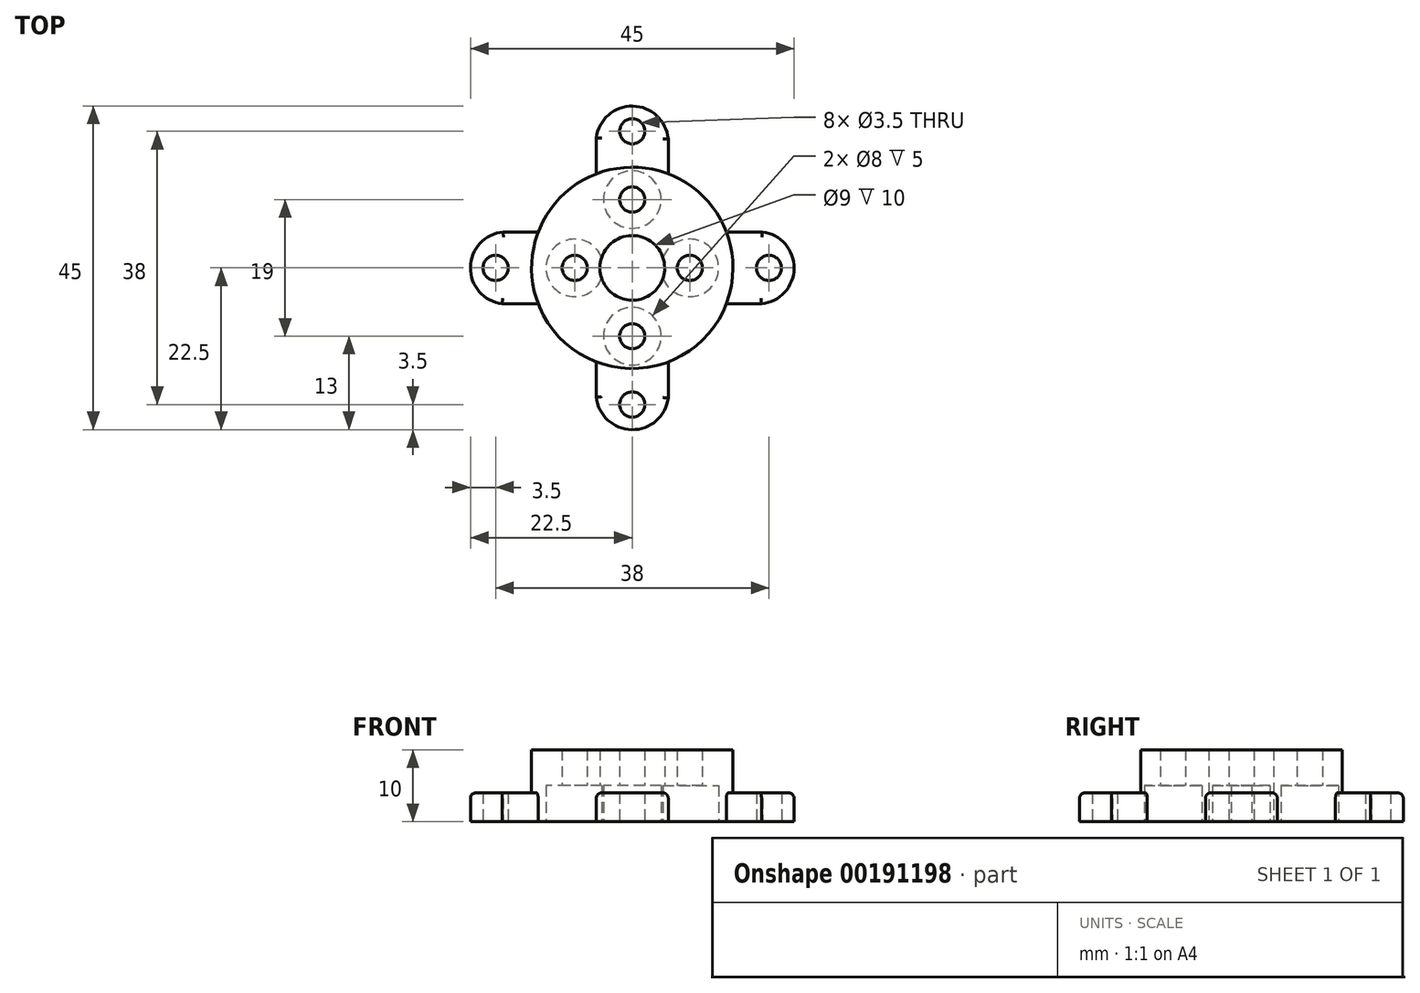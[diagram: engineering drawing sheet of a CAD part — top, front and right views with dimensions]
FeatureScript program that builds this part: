
annotation { "Feature Type Name" : "Feature", "Feature Type Description" : "" }
export const myFeature = defineFeature(function(context is Context, id is Id, definition is map)
    precondition{}
    {
        {
            var Q0;
            Q0=qCreatedBy(makeId("Top.planeOp"),FACE);
            var sketch = newSketch(context, id + "F0", { "sketchPlane" : qUnion([Q0])});
            skCircle(sketch, "E0", {"center": v(0, 0) * mm, "radius": 14 * mm});
            skCircle(sketch, "E1", {"center": v(0, 9.5) * mm, "radius": 1.75 * mm});
            skCircle(sketch, "E2", {"center": v(8, 0) * mm, "radius": 1.75 * mm});
            skCircle(sketch, "E3", {"center": v(0, -9.5) * mm, "radius": 1.75 * mm});
            skCircle(sketch, "E4", {"center": v(-8, 0) * mm, "radius": 1.75 * mm});
            skLineSegment(sketch, "E5", {"start": v(-22.5, 0) * mm, "end": v(-22.5, 0) * mm});
            skCircle(sketch, "E6", {"center": v(-19, 0) * mm, "radius": 1.75 * mm});
            skCircle(sketch, "E7", {"center": v(19, 0) * mm, "radius": 1.75 * mm});
            skCircle(sketch, "E8", {"center": v(0, 19) * mm, "radius": 1.75 * mm});
            skCircle(sketch, "E9", {"center": v(0, -19) * mm, "radius": 1.75 * mm});
            skLineSegment(sketch, "E10", {"start": v(0, 0) * mm, "end": v(-22.5, 0) * mm});
            skLineSegment(sketch, "E11.0", {"start": v(-13.08, 5) * mm, "end": v(-17.95, 5) * mm});
            skLineSegment(sketch, "E12.0", {"start": v(-13.08, -5) * mm, "end": v(-18.08, -5) * mm});
            skArc(sketch, "E13", {"start": v(-17, 5) * mm, "mid": v(-22.5, -0.07) * mm, "end": v(-16.86, -5) * mm});
            skPoint(sketch, "E13.second.point", {"position": v(-18.08, -5) * mm});
            skPoint(sketch, "E13.third.point", {"position": v(-17.95, 5) * mm});
            skLineSegment(sketch, "E14.trimOffspring", {"start": v(-21.94, 5) * mm, "end": v(-22.5, 5) * mm});
            skLineSegment(sketch, "E15.trimOffspring", {"start": v(-21.94, -5) * mm, "end": v(-22.5, -5) * mm});
            skLineSegment(sketch, "E16.1.0", {"start": v(-5, -13.08) * mm, "end": v(-5, -17.95) * mm});
            skLineSegment(sketch, "E16.1.1", {"start": v(5, -13.08) * mm, "end": v(5, -18.08) * mm});
            skArc(sketch, "E16.1.2", {"start": v(-5, -17) * mm, "mid": v(0.07, -22.5) * mm, "end": v(5, -16.86) * mm});
            skLineSegment(sketch, "E16.2.0", {"start": v(13.08, -5) * mm, "end": v(17.95, -5) * mm});
            skLineSegment(sketch, "E16.2.1", {"start": v(13.08, 5) * mm, "end": v(18.08, 5) * mm});
            skArc(sketch, "E16.2.2", {"start": v(17, -5) * mm, "mid": v(22.5, 0.07) * mm, "end": v(16.86, 5) * mm});
            skLineSegment(sketch, "E16.3.0", {"start": v(5, 13.08) * mm, "end": v(5, 17.95) * mm});
            skLineSegment(sketch, "E16.3.1", {"start": v(-5, 13.08) * mm, "end": v(-5, 18.08) * mm});
            skArc(sketch, "E16.3.2", {"start": v(5, 17) * mm, "mid": v(-0.07, 22.5) * mm, "end": v(-5, 16.86) * mm});
            skCircle(sketch, "E17", {"center": v(0, 0) * mm, "radius": 4.5 * mm});
            skSolve(sketch);
        }
        {
            var Q0;
            Q0=makeQuery(id+"F0.imprint","IMPRINT",FACE,{"disambiguationData":[TD([[makeQuery(id+"F0.imprint","IMPRINT",EDGE,{"derivedFrom":sQuery(id+"F0.wireOp",EDGE,"E1")}),-1.0]])]});
            extrude(context, id + "F1", {"entities" : qUnion([Q0]), "depth" : 10 * mm});
        }
        {
            var Q0;
            Q0=makeQuery(id+"F0.imprint","IMPRINT",FACE,{"disambiguationData":[TD([[makeQuery(id+"F0.imprint","IMPRINT",EDGE,{"derivedFrom":sQuery(id+"F0.wireOp",EDGE,"E8")}),-1.0]])]});
            var Q1;
            Q1=makeQuery(id+"F0.imprint","IMPRINT",FACE,{"disambiguationData":[TD([[makeQuery(id+"F0.imprint","IMPRINT",EDGE,{"derivedFrom":sQuery(id+"F0.wireOp",EDGE,"E7")}),-1.0]])]});
            var Q2;
            Q2=makeQuery(id+"F0.imprint","IMPRINT",FACE,{"disambiguationData":[TD([[makeQuery(id+"F0.imprint","IMPRINT",EDGE,{"derivedFrom":sQuery(id+"F0.wireOp",EDGE,"E9")}),-1.0]])]});
            var Q3;
            {var subQ5=sQuery(id+"F0.wireOp",EDGE,"E12.0");var subQ9=sQuery(id+"F0.wireOp",EDGE,"E0");var subQ11=makeQuery(id+"F0.imprint","INTERSECT",VERTEX,{"derivedFrom":[subQ9,subQ5]});Q3=makeQuery(id+"F0.imprint","IMPRINT",FACE,{"disambiguationData":[TD([[makeQuery(id+"F0.imprint","IMPRINT",EDGE,{"disambiguationData":[TD([[subQ11,1.0]])],"derivedFrom":subQ9}),-1.0]])]});}
            var Q4;
            {var subQ5=sQuery(id+"F0.wireOp",EDGE,"E11.0");var subQ6=sQuery(id+"F0.wireOp",EDGE,"E0");var subQ7=makeQuery(id+"F0.imprint","INTERSECT",VERTEX,{"derivedFrom":[subQ6,subQ5]});Q4=makeQuery(id+"F0.imprint","IMPRINT",FACE,{"disambiguationData":[TD([[makeQuery(id+"F0.imprint","IMPRINT",EDGE,{"disambiguationData":[TD([[subQ7,-1.0]])],"derivedFrom":subQ6}),-1.0]])]});}
            extrude(context, id + "F2", {"entities" : qUnion([Q0, Q1, Q2, Q3, Q4]), "operationType" : NewBodyOperationType.ADD, "depth" : 4 * mm});
        }
        {
            var Q0;
            Q0=qCreatedBy(makeId("Top.planeOp"),FACE);
            var sketch = newSketch(context, id + "F3", { "sketchPlane" : qUnion([Q0])});
            skCircle(sketch, "E18.0", {"center": v(-8, 0) * mm, "radius": 1.75 * mm});
            skCircle(sketch, "E18.1", {"center": v(0, 9.5) * mm, "radius": 1.75 * mm});
            skCircle(sketch, "E18.2", {"center": v(8, 0) * mm, "radius": 1.75 * mm});
            skCircle(sketch, "E18.3", {"center": v(0, -9.5) * mm, "radius": 1.75 * mm});
            skCircle(sketch, "E19", {"center": v(0, 9.5) * mm, "radius": 4 * mm});
            skCircle(sketch, "E20", {"center": v(8, 0) * mm, "radius": 4 * mm});
            skCircle(sketch, "E21", {"center": v(0, -9.5) * mm, "radius": 4 * mm});
            skCircle(sketch, "E22", {"center": v(-8, 0) * mm, "radius": 4 * mm});
            skSolve(sketch);
        }
        {
            var Q0;
            Q0=makeQuery(id+"F3.imprint","IMPRINT",FACE,{"disambiguationData":[TD([[makeQuery(id+"F3.imprint","IMPRINT",EDGE,{"derivedFrom":sQuery(id+"F3.wireOp",EDGE,"E18.1")}),-1.0]])]});
            var Q1;
            Q1=makeQuery(id+"F3.imprint","IMPRINT",FACE,{"disambiguationData":[TD([[makeQuery(id+"F3.imprint","IMPRINT",EDGE,{"derivedFrom":sQuery(id+"F3.wireOp",EDGE,"E18.2")}),-1.0]])]});
            var Q2;
            Q2=makeQuery(id+"F3.imprint","IMPRINT",FACE,{"disambiguationData":[TD([[makeQuery(id+"F3.imprint","IMPRINT",EDGE,{"derivedFrom":sQuery(id+"F3.wireOp",EDGE,"E18.3")}),-1.0]])]});
            var Q3;
            Q3=makeQuery(id+"F3.imprint","IMPRINT",FACE,{"disambiguationData":[TD([[makeQuery(id+"F3.imprint","IMPRINT",EDGE,{"derivedFrom":sQuery(id+"F3.wireOp",EDGE,"E18.0")}),-1.0]])]});
            extrude(context, id + "F4", {"entities" : qUnion([Q0, Q1, Q2, Q3]), "operationType" : NewBodyOperationType.REMOVE, "depth" : 5 * mm});
        }
        {
            var Q0;
            Q0=makeQuery(id+"F2.opExtrude","CAP_EDGE",EDGE,{"disambiguationData":[OSD([sQuery(id+"F0.wireOp",EDGE,"E16.1.0")])],"isStart":false});
            var Q1;
            Q1=makeQuery(id+"F2.opExtrude","CAP_EDGE",EDGE,{"disambiguationData":[OSD([sQuery(id+"F0.wireOp",EDGE,"E16.1.2")])],"isStart":false});
            var Q2;
            Q2=makeQuery(id+"F2.opExtrude","CAP_EDGE",EDGE,{"disambiguationData":[OSD([sQuery(id+"F0.wireOp",EDGE,"E16.1.1")])],"isStart":false});
            var Q3;
            Q3=makeQuery(id+"F2.opExtrude","CAP_EDGE",EDGE,{"disambiguationData":[OSD([sQuery(id+"F0.wireOp",EDGE,"E16.2.0")])],"isStart":false});
            var Q4;
            Q4=makeQuery(id+"F2.opExtrude","CAP_EDGE",EDGE,{"disambiguationData":[OSD([sQuery(id+"F0.wireOp",EDGE,"E16.2.2")])],"isStart":false});
            var Q5;
            Q5=makeQuery(id+"F2.opExtrude","CAP_EDGE",EDGE,{"disambiguationData":[OSD([sQuery(id+"F0.wireOp",EDGE,"E16.2.1")])],"isStart":false});
            var Q6;
            Q6=makeQuery(id+"F2.opExtrude","CAP_EDGE",EDGE,{"disambiguationData":[OSD([sQuery(id+"F0.wireOp",EDGE,"E16.3.0")])],"isStart":false});
            var Q7;
            Q7=makeQuery(id+"F2.opExtrude","CAP_EDGE",EDGE,{"disambiguationData":[OSD([sQuery(id+"F0.wireOp",EDGE,"E16.3.2")])],"isStart":false});
            var Q8;
            Q8=makeQuery(id+"F2.opExtrude","CAP_EDGE",EDGE,{"disambiguationData":[OSD([sQuery(id+"F0.wireOp",EDGE,"E16.3.1")])],"isStart":false});
            var Q9;
            Q9=makeQuery(id+"F2.opExtrude","CAP_EDGE",EDGE,{"disambiguationData":[OSD([sQuery(id+"F0.wireOp",EDGE,"E11.0")])],"isStart":false});
            var Q10;
            Q10=makeQuery(id+"F2.opExtrude","CAP_EDGE",EDGE,{"disambiguationData":[OSD([sQuery(id+"F0.wireOp",EDGE,"E13")])],"isStart":false});
            var Q11;
            Q11=makeQuery(id+"F2.opExtrude","CAP_EDGE",EDGE,{"disambiguationData":[OSD([sQuery(id+"F0.wireOp",EDGE,"E12.0")])],"isStart":false});
            fillet(context, id + "F5", {"entities" : qUnion([Q0, Q1, Q2, Q3, Q4, Q5, Q6, Q7, Q8, Q9, Q10, Q11]), "radius" : .75 * mm, "tangentPropagation" : true, "allowEdgeOverflow" : false});
        }
    });
